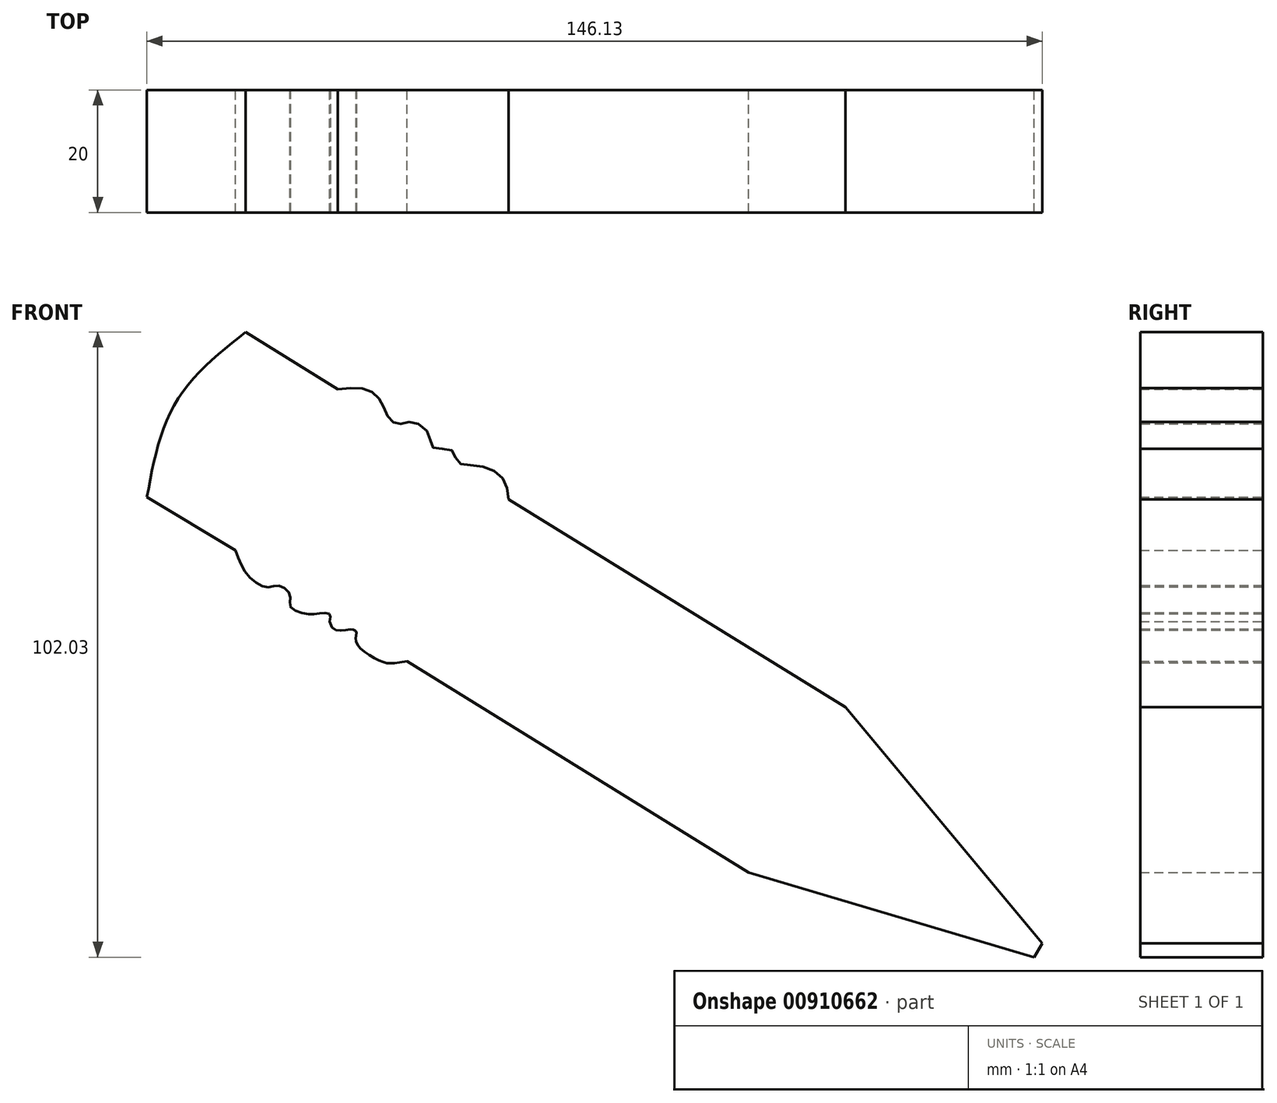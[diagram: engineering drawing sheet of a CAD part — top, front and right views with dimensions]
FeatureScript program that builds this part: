
annotation { "Feature Type Name" : "Feature", "Feature Type Description" : "" }
export const myFeature = defineFeature(function(context is Context, id is Id, definition is map)
    precondition{}
    {
        {
            var Q0;
            Q0=qCreatedBy(makeId("Front.planeOp"),FACE);
            var sketch = newSketch(context, id + "F0", { "sketchPlane" : qUnion([Q0])});
            skFitSpline(sketch, "E0", {"points": [v(-88.83, 26.77) * mm, v(-84.07, 42.35) * mm, v(-72.7, 53.72) * mm], "startDerivative": vector(6.16, 33.13) * mm, "endDerivative": vector(26.13, 20.76) * mm});
            skLineSegment(sketch, "E1", {"start": v(-72.7, 53.72) * mm, "end": v(-57.66, 44.37) * mm});
            skFitSpline(sketch, "E2", {"points": [v(-57.66, 44.37) * mm, v(-53.08, 44.37) * mm, v(-50.7, 42.54) * mm, v(-49.41, 39.79) * mm, v(-47.76, 38.69) * mm, v(-45.56, 39.05) * mm, v(-42.81, 37.04) * mm, v(-42.08, 34.84) * mm, v(-39.15, 34.47) * mm, v(-38.05, 32.45) * mm, v(-34.93, 31.9) * mm, v(-30.9, 30.07) * mm, v(-29.8, 26.4) * mm], "startDerivative": vector(48.36, 5.43) * mm, "endDerivative": vector(4.76, -43.25) * mm});
            skLineSegment(sketch, "E3", {"start": v(-29.8, 26.4) * mm, "end": v(25.21, -7.52) * mm});
            skLineSegment(sketch, "E4", {"start": v(25.21, -7.52) * mm, "end": v(57.3, -46.02) * mm});
            skLineSegment(sketch, "E5", {"start": v(57.3, -46.02) * mm, "end": v(56.01, -48.31) * mm});
            skLineSegment(sketch, "E6", {"start": v(56.01, -48.31) * mm, "end": v(9.35, -34.47) * mm});
            skLineSegment(sketch, "E7", {"start": v(9.35, -34.47) * mm, "end": v(-46.39, 0) * mm});
            skFitSpline(sketch, "E8", {"points": [v(-46.39, 0) * mm, v(-50.6, 0) * mm, v(-54.64, 2.98) * mm, v(-54.64, 4.63) * mm, v(-55.55, 5.18) * mm, v(-59, 6.49) * mm], "startDerivative": vector(-31.03, -5.4) * mm, "endDerivative": vector(-5.52, 29) * mm});
            skFitSpline(sketch, "E9", {"points": [v(-59, 6.49) * mm, v(-59, 7.7) * mm, v(-60.53, 7.81) * mm, v(-62.82, 7.7) * mm, v(-65.43, 8.9) * mm, v(-65.43, 10.75) * mm, v(-67.18, 12.28) * mm, v(-69.36, 12.06) * mm, v(-72.52, 14.24) * mm, v(-74.37, 18.06) * mm], "startDerivative": vector(4.2, 18.66) * mm, "endDerivative": vector(-9.6, 26.88) * mm});
            skLineSegment(sketch, "E10", {"start": v(-88.83, 26.77) * mm, "end": v(-74.37, 18.06) * mm});
            skSolve(sketch);
        }
        {
            var Q0;
            Q0 = qSketchRegion(id + "F0", true);
            extrude(context, id + "F1", {"entities" : qUnion([Q0]), "depth" : 20 * mm, "offsetDistance" : 25 * mm});
        }
    });
